# Revit family: 142096-Lipumax NS 7
name_source: partatom
category: Plumbing Fixtures
revit_build: Autodesk Revit 2016 (Build: 20150220_1215(x64)
units: mm (PartAtom-declared; Revit-internal decimal feet)

## family parameters
Always vertical = Yes
Cut with Voids When Loaded = No
Host = Floor
Part Type = Normal
Room Calculation Point = No
Round Connector Dimension = Use Diameter
Shared = No
Work Plane-Based = No

## types (8) — shared parameters
Assembly Code = D2030400
Baffle cap to suit NS 2-4 product code 142105 = 2 xBaffle cap 190Ø x  68 high. Black plastic and rubber 0.1kg
Collar and/or load distribution plate = Reinforced Concrete
Fax = +44 (2) 4747 4040
Flow distributor 110Ø product code 142101 = 110Ø. Black HDPE pipe, 0.6kg
Flow distributor 160Ø product code 142102 = 160Ø. Black HDPE pipe, 1.3kg
Flow rate = 7 L/s out flow of treated effluent to EN 1825
Grease separator body material = Polyethylene
Installation guidelines = www.acopassavant.com.au/resources/technical-data
Load distribution plate product code 142311 = 733kg
Maintenance guidelines = www.acopassavant.com.au/resources/installation
Manufacturer = ACO Polycrete Pty Ltd
Model = ACO Passavant Lipumax NS 7 / 1675 L
Model Description = Below ground gravity grease separator
Price = 0.00
Product Code = 142096
Product Dimensions = 1321 x 2316
Product Page URL = www.acopassavant.com.au
Product Standard = EN 1825
Product Weight = 108
Product brochure = www.acopassavant.com.au/resources
Revision = 0
Telephone = +61 (0) 2 4747 4000
Type Comments = ACO Passavant Lipumax NS 7 / 1675 L
URL = www.acopassavant.com.au
zero-valued in all types: Cost

## per-type parameters (varying)
| type | Class B | Class D | Cover Depth | GCW | Grease separator lid material | Riser tube product code 142134 | Riser tube product code 142350 |
| 142096-Lipumax with (142120-Rhinocast Class B circular cover, R C collar) | Yes | No | 130 mm  [stored 0.426509 ft] | No | ACOIron, Ductile |  | Adds between 367-607mm to overall height. 22kg |
| 142096-Lipumax with (142137-GCW Rhinocast Class D circular cover, R C collar, load distr. plate & GCW riser) | No | Yes | 180 mm  [stored 0.590551 ft] | Yes | ACOIron, Ductile | Adds between 367-607mm to overall height |  |
| 142096-Lipumax with (142138-GCW SAKU Class B circular cover, R C collar and GCW riser) | Yes | No | 130 mm  [stored 0.426509 ft] | Yes | ACO Polypropylene | Adds between 367-607mm to overall height |  |
| 142096-Lipumax with (142299-Rhinocast Class D circular cover, R C collar, load distr. plate & riser) | No | Yes | 180 mm  [stored 0.590551 ft] | No | ACOIron, Ductile |  | Adds between 367-607mm to overall height. 22kg |
| 142096-Lipumax with (142099-Rhinocast Class D circular cover, R C collar) | No | Yes | 180 mm  [stored 0.590551 ft] | No | ACOIron, Ductile |  | Adds between 367-607mm to overall height. 22kg |
| 142096-Lipumax with (142155-GCW Rhinocast Class D circular cover, R C collar and GCW riser) | No | Yes | 180 mm  [stored 0.590551 ft] | Yes | ACOIron, Ductile | Adds between 367-607mm to overall height |  |
| 142096-Lipumax with (142139-GCW Rhinocast Class B circular cover, R C collar and GCW riser) | Yes | No | 130 mm  [stored 0.426509 ft] | Yes | ACOIron, Ductile | Adds between 367-607mm to overall height |  |
| 142096-Lipumax with (142119-SAKU Class B circular cover, R C collar) | Yes | No | 130 mm  [stored 0.426509 ft] | No | ACO Polypropylene |  | Adds between 367-607mm to overall height. 22kg |

note: [stored X ft] marks values corroborated as IEEE doubles in the binary element streams (Revit-internal decimal feet)

## geometry (parser evidence)
native form markers: Sweep x6
no freeform markers — native parametric forms only
